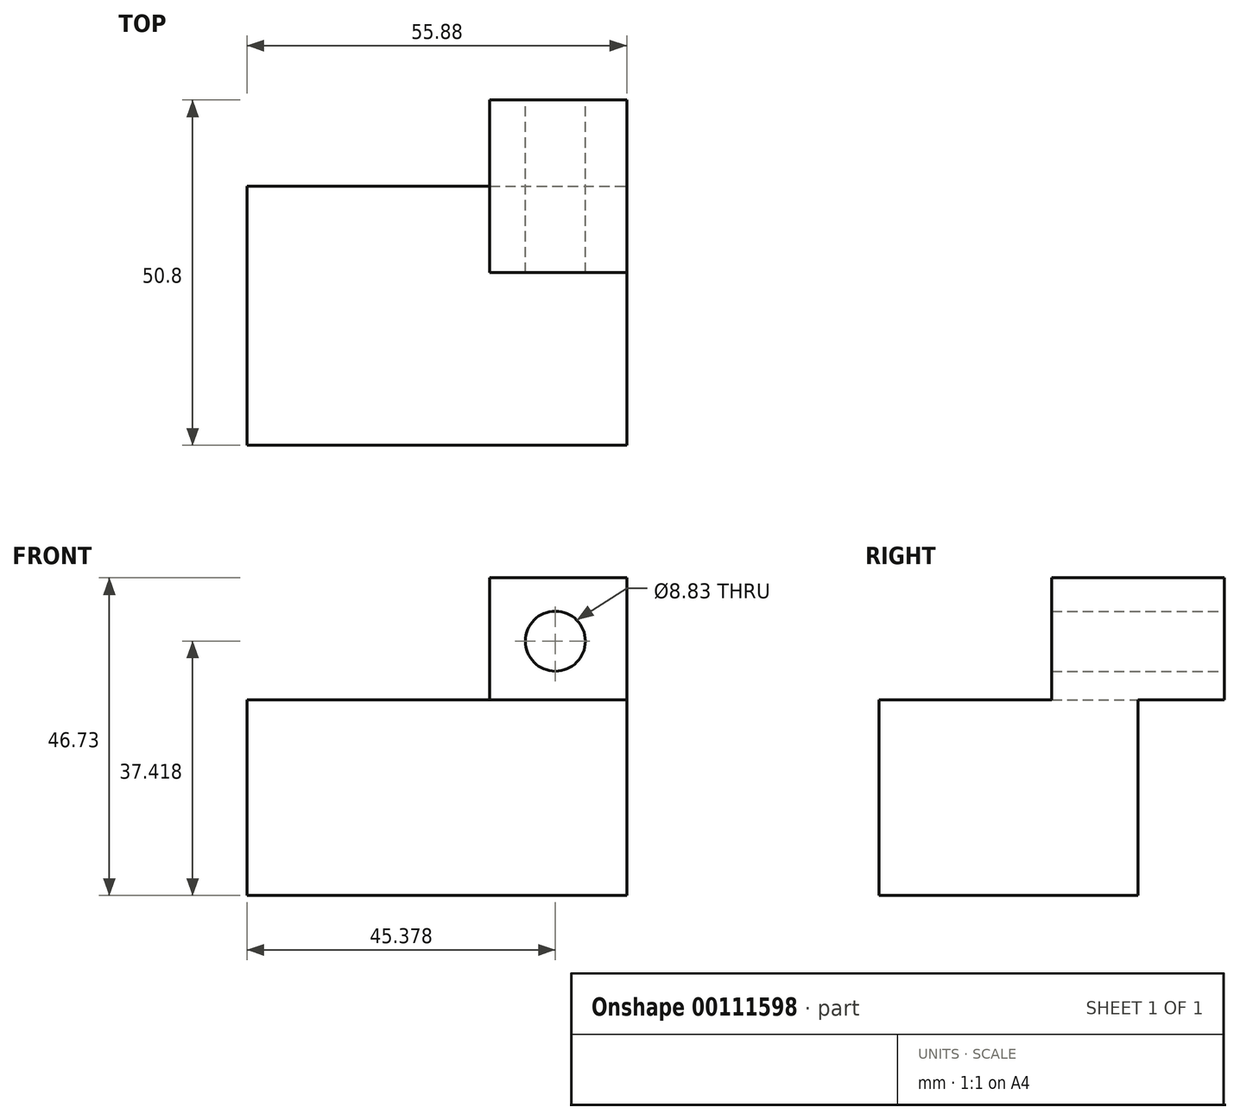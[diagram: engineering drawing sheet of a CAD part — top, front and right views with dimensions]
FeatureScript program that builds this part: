
annotation { "Feature Type Name" : "Feature", "Feature Type Description" : "" }
export const myFeature = defineFeature(function(context is Context, id is Id, definition is map)
    precondition{}
    {
        {
            var Q0;
            Q0=qCreatedBy(makeId("Front.planeOp"),FACE);
            var sketch = newSketch(context, id + "F0", { "sketchPlane" : qUnion([Q0])});
            skLineSegment(sketch, "E0.bottom", {"start": v(-19.47, 13.46) * mm, "end": v(36.4, 13.46) * mm});
            skLineSegment(sketch, "E0.top", {"start": v(-19.47, -15.32) * mm, "end": v(36.4, -15.32) * mm});
            skLineSegment(sketch, "E0.left", {"start": v(-19.47, 13.46) * mm, "end": v(-19.47, -15.32) * mm});
            skLineSegment(sketch, "E0.right", {"start": v(36.4, 13.46) * mm, "end": v(36.4, -15.32) * mm});
            skLineSegment(sketch, "E1.bottom", {"start": v(16.26, 31.41) * mm, "end": v(36.4, 31.41) * mm});
            skLineSegment(sketch, "E1.top", {"start": v(16.26, 13.46) * mm, "end": v(36.4, 13.46) * mm});
            skLineSegment(sketch, "E1.left", {"start": v(16.26, 31.41) * mm, "end": v(16.26, 13.46) * mm});
            skLineSegment(sketch, "E1.right", {"start": v(36.4, 31.41) * mm, "end": v(36.4, 13.46) * mm});
            skCircle(sketch, "E2", {"center": v(25.9, 22.1) * mm, "radius": 4.42 * mm});
            skSolve(sketch);
        }
        {
            var Q0;
            Q0=makeQuery(id+"F0.imprint","IMPRINT",FACE,{"disambiguationData":[TD([[makeQuery(id+"F0.imprint","IMPRINT",EDGE,{"derivedFrom":sQuery(id+"F0.wireOp",EDGE,"E1.bottom")}),-1.0]])]});
            extrude(context, id + "F1", {"entities" : qUnion([Q0]), "endBound" : BoundingType.SYMMETRIC, "depth" : 25.4 * mm});
        }
        {
            var Q0;
            Q0=makeQuery(id+"F0.imprint","IMPRINT",FACE,{"disambiguationData":[TD([[makeQuery(id+"F0.imprint","IMPRINT",EDGE,{"derivedFrom":sQuery(id+"F0.wireOp",EDGE,"E0.bottom")}),-1.0]])]});
            extrude(context, id + "F2", {"entities" : qUnion([Q0]), "operationType" : NewBodyOperationType.ADD, "depth" : 38.1 * mm});
        }
    });
